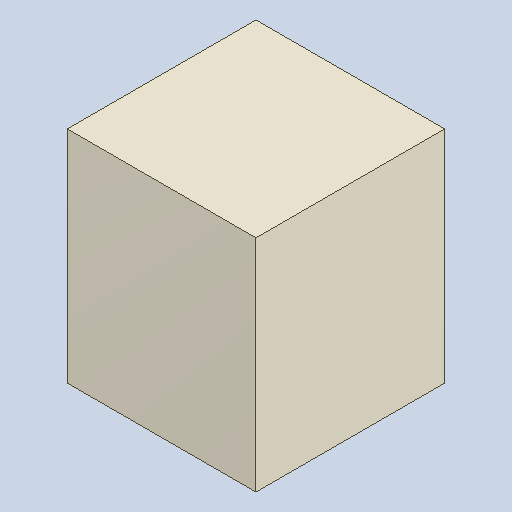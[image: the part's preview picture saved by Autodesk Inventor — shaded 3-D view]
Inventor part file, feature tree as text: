
AUTODESK INVENTOR PART (.ipt)
format: ipt  version: 2023.4 (Build 274418000, 418)  size: 82,944 bytes
history: native  units: mm
features: extrude x1
ambient origin geometry x8: Origin, YZ Plane, XZ Plane, XY Plane, X Axis, Y Axis, Z Axis, Center Point
bodies: Solid1 (feature_tree)
feature tree (1):
  extrude  "Extruded_20"  [1 undecoded]
note: 1 required parameter value undecoded (feature->parameter linkage not recoverable at this tier; creation-order binding heuristic only, values carry confidence <= 0.55)
